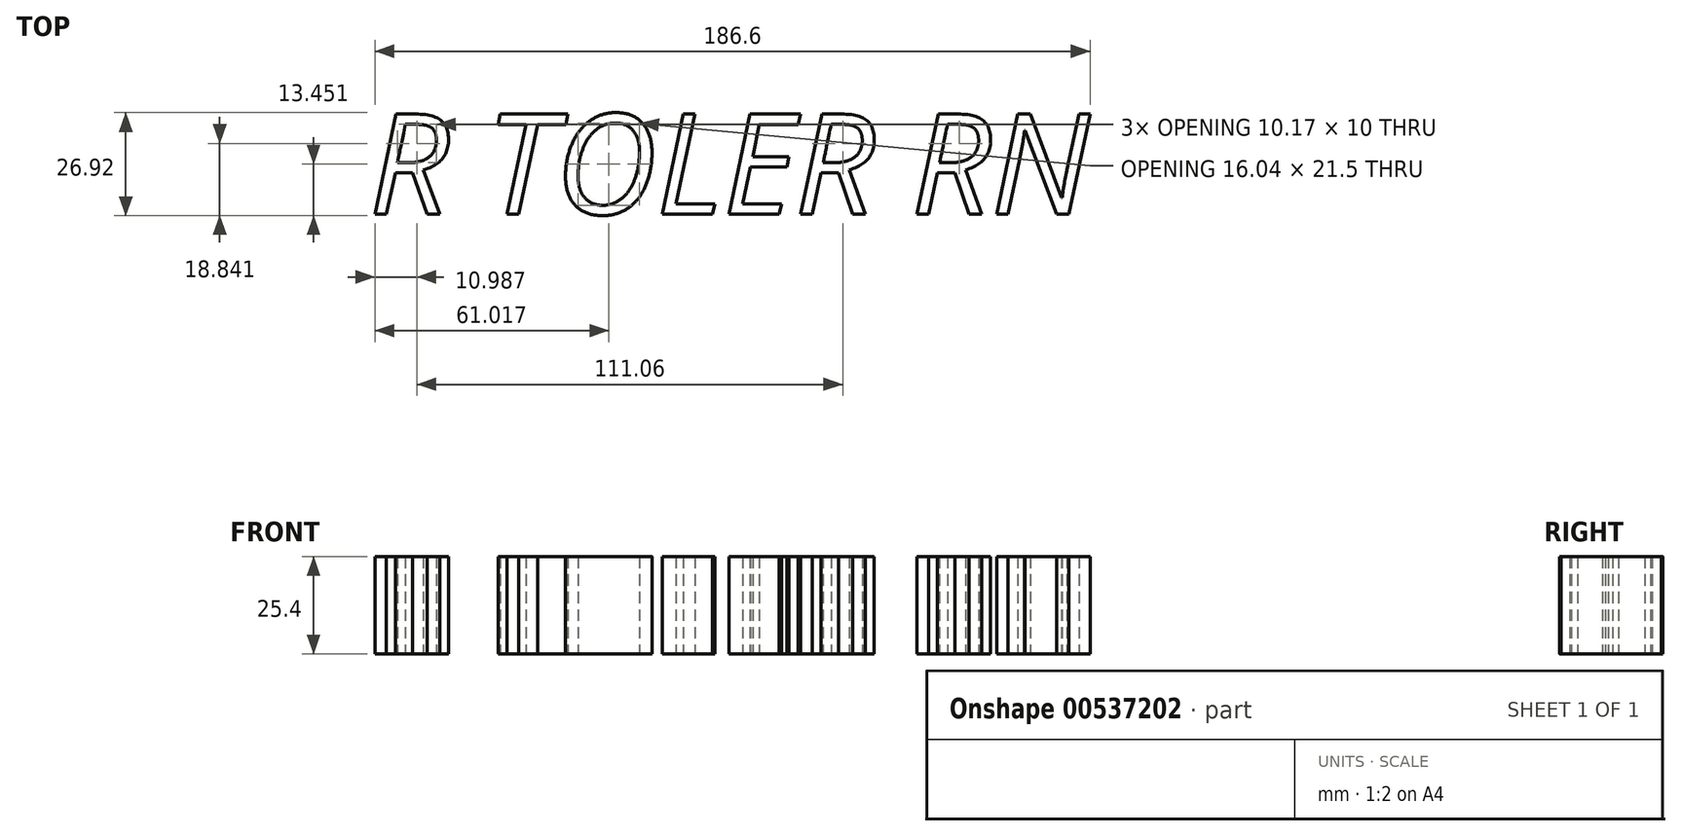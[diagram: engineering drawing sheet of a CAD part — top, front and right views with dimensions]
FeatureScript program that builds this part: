
annotation { "Feature Type Name" : "Feature", "Feature Type Description" : "" }
export const myFeature = defineFeature(function(context is Context, id is Id, definition is map)
    precondition{}
    {
        {
            var Q0;
            Q0=qCreatedBy(makeId("Top.planeOp"),FACE);
            var sketch = newSketch(context, id + "F0", { "sketchPlane" : qUnion([Q0])});
            skText(sketch, "E0", { "text": "R TOLER RN", "fontName": "OpenSans-Italic.ttf"});
            const initialGuessF0  = {"E0": [-0.0308, -0.01406, 1, 0, 0.02637]};
            skSetInitialGuess(sketch, initialGuessF0);
            skSolve(sketch);
        }
        {
            var Q0;
            Q0 = qSketchRegion(id + "F0", true);
            extrude(context, id + "F1", {"entities" : qUnion([Q0]), "depth" : 25.4 * mm, "offsetDistance" : 25.4 * mm});
        }
    });
